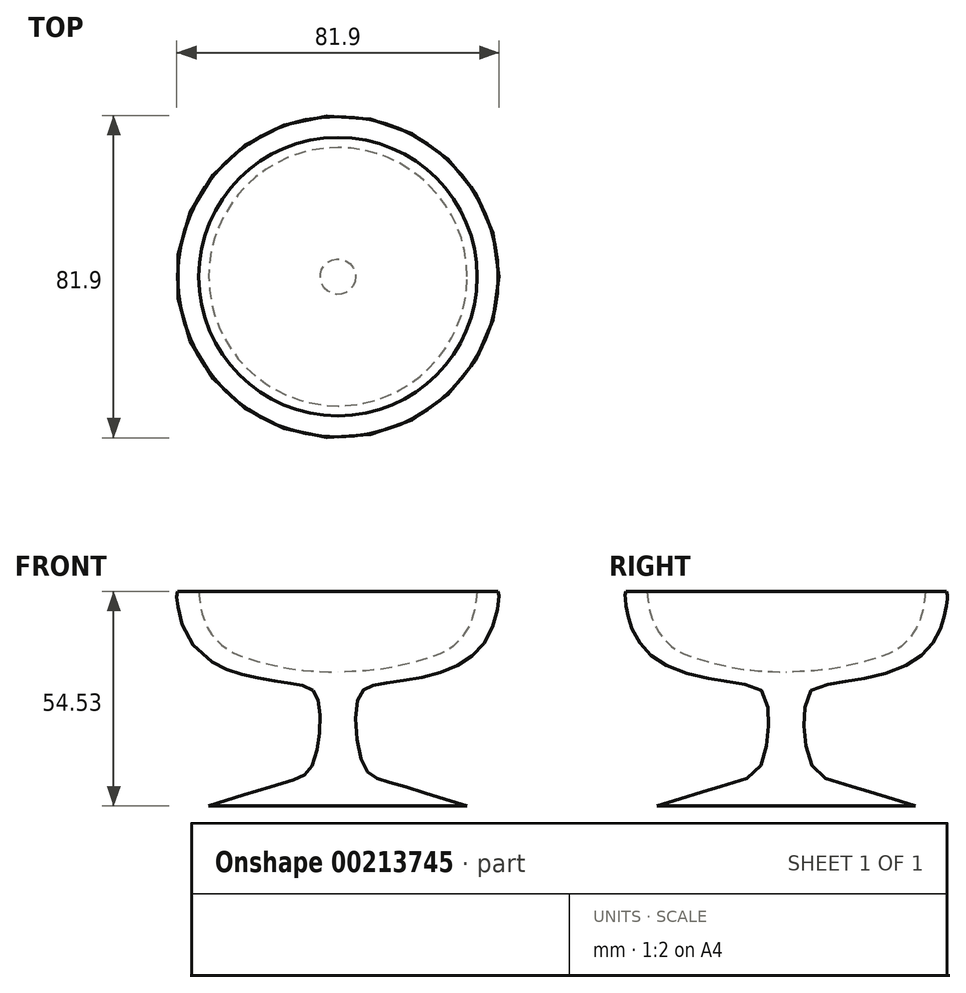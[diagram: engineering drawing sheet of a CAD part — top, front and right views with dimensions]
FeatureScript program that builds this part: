
annotation { "Feature Type Name" : "Feature", "Feature Type Description" : "" }
export const myFeature = defineFeature(function(context is Context, id is Id, definition is map)
    precondition{}
    {
        {
            var Q0;
            Q0=qCreatedBy(makeId("Front.planeOp"),FACE);
            var sketch = newSketch(context, id + "F0", { "sketchPlane" : qUnion([Q0])});
            skLineSegment(sketch, "E0", {"start": v(0, 0) * mm, "end": v(-26.94, 0) * mm});
            skLineSegment(sketch, "E1", {"start": v(-26.94, 0) * mm, "end": v(-32.81, 0) * mm});
            skFitSpline(sketch, "E2", {"points": [v(-32.81, 0) * mm, v(-12.83, 6.14) * mm, v(-6.6, 10.17) * mm, v(-5.32, 27.77) * mm, v(-10.26, 30.89) * mm, v(-26.21, 34) * mm, v(-38.5, 43.53) * mm, v(-40.88, 54.35) * mm, v(-40.7, 54.53) * mm], "startDerivative": vector(127.46, 40.04) * mm, "endDerivative": vector(10.36, 3.54) * mm});
            skLineSegment(sketch, "E3", {"start": v(-40.7, 54.53) * mm, "end": v(-35.38, 54.53) * mm});
            skFitSpline(sketch, "E4", {"points": [v(-35.38, 54.53) * mm, v(-34.1, 47.57) * mm, v(-30.43, 41.7) * mm, v(-24.93, 38.22) * mm, v(-15.76, 35.65) * mm, v(-9.35, 34.55) * mm, v(0, 34) * mm], "startDerivative": vector(4.54, -44.1) * mm, "endDerivative": vector(53.87, -2.13) * mm});
            skLineSegment(sketch, "E5", {"start": v(0, 34) * mm, "end": v(0, 0) * mm});
            skSolve(sketch);
        }
        {
            var Q0;
            Q0=makeQuery(id+"F0.imprint","IMPRINT",FACE,{"disambiguationData":[TD([[makeQuery(id+"F0.imprint","IMPRINT",EDGE,{"derivedFrom":sQuery(id+"F0.wireOp",EDGE,"E0")}),-1.0]])]});
            var Q1;
            Q1=sQuery(id+"F0.wireOp",EDGE,"E5");
            revolve(context, id + "F1", {"entities" : qUnion([Q0]), "axis" : qUnion([Q1]), "revolveType" : RevolveType.FULL});
        }
    });
